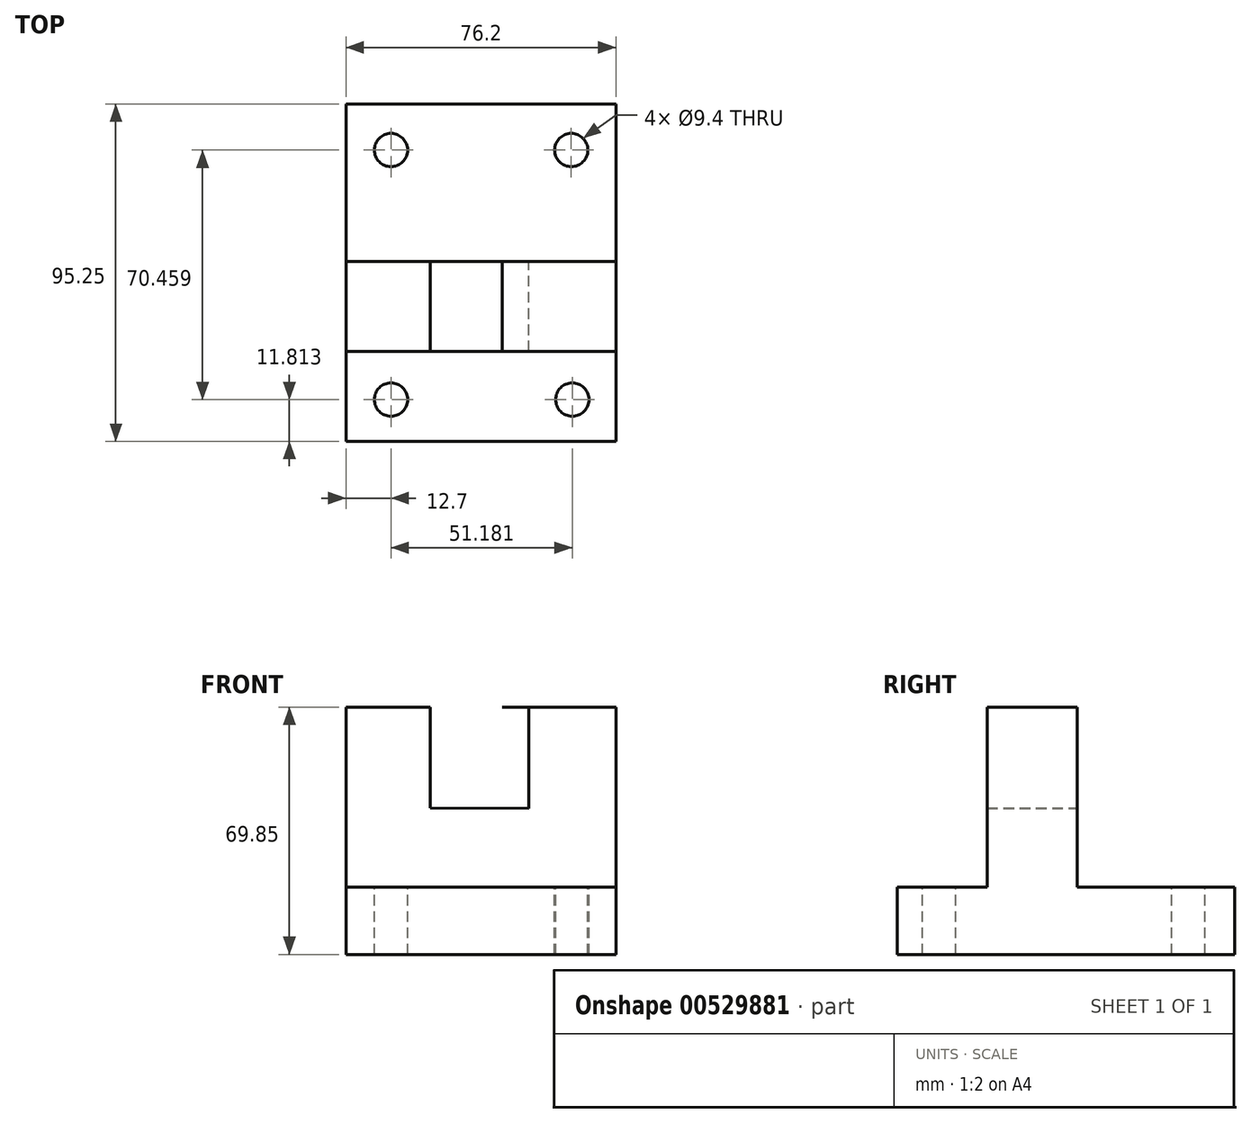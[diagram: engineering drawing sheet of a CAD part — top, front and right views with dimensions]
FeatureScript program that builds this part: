
annotation { "Feature Type Name" : "Feature", "Feature Type Description" : "" }
export const myFeature = defineFeature(function(context is Context, id is Id, definition is map)
    precondition{}
    {
        {
            var Q0;
            Q0=qCreatedBy(makeId("Right.planeOp"),FACE);
            var sketch = newSketch(context, id + "F0", { "sketchPlane" : qUnion([Q0])});
            skPoint(sketch, "E0.start.orphan", {"position": v(-46.47, 48.09) * mm});
            skPoint(sketch, "E1.start.orphan", {"position": v(-22.64, 19.51) * mm});
            skPoint(sketch, "E2.end.orphan", {"position": v(5.9, 19.51) * mm});
            skPoint(sketch, "E3.end.orphan", {"position": v(29.73, 48.09) * mm});
            skLineSegment(sketch, "E4", {"start": v(44.45, -31.82) * mm, "end": v(-50.8, -31.82) * mm});
            skLineSegment(sketch, "E5", {"start": v(-50.8, -31.82) * mm, "end": v(-50.8, -12.77) * mm});
            skLineSegment(sketch, "E6", {"start": v(-50.8, -12.77) * mm, "end": v(-25.4, -12.77) * mm});
            skLineSegment(sketch, "E7", {"start": v(-25.4, -12.77) * mm, "end": v(-25.4, 38.03) * mm});
            skLineSegment(sketch, "E8", {"start": v(-25.4, 38.03) * mm, "end": v(0, 38.03) * mm});
            skLineSegment(sketch, "E9", {"start": v(0, 38.03) * mm, "end": v(0, -12.77) * mm});
            skLineSegment(sketch, "E10", {"start": v(0, -12.77) * mm, "end": v(44.45, -12.77) * mm});
            skLineSegment(sketch, "E11", {"start": v(44.45, -12.77) * mm, "end": v(44.45, -31.82) * mm});
            skSolve(sketch);
        }
        {
            var Q0;
            Q0=makeQuery(id+"F0.imprint","IMPRINT",FACE,{"disambiguationData":[TD([[makeQuery(id+"F0.imprint","IMPRINT",EDGE,{"derivedFrom":sQuery(id+"F0.wireOp",EDGE,"E4")}),-1.0]])]});
            extrude(context, id + "F1", {"entities" : qUnion([Q0]), "depth" : 76.2 * mm, "offsetDistance" : 25.4 * mm});
        }
        {
            var Q0;
            Q0=qCreatedBy(makeId("Front.planeOp"),FACE);
            var sketch = newSketch(context, id + "F2", { "sketchPlane" : qUnion([Q0])});
            skLineSegment(sketch, "E12", {"start": v(51.64, 38.02) * mm, "end": v(51.64, 9.44) * mm});
            skLineSegment(sketch, "E13", {"start": v(0, 38.08) * mm, "end": v(23.83, 38.08) * mm});
            skLineSegment(sketch, "E14", {"start": v(51.64, 38.02) * mm, "end": v(23.83, 38.08) * mm});
            skLineSegment(sketch, "E15", {"start": v(23.83, 38.08) * mm, "end": v(23.83, 9.5) * mm});
            skLineSegment(sketch, "E16", {"start": v(51.64, 9.44) * mm, "end": v(23.83, 9.5) * mm});
            skPoint(sketch, "E17.end.orphan", {"position": v(23.83, 24.1) * mm});
            skLineSegment(sketch, "E18", {"start": v(23.83, 38.08) * mm, "end": v(0, 38.08) * mm});
            skLineSegment(sketch, "E19", {"start": v(75.47, 38.05) * mm, "end": v(51.64, 38.02) * mm});
            skPoint(sketch, "E19.startSnap0", {"position": v(37.73, 38.05) * mm});
            skLineSegment(sketch, "E20", {"start": v(75.8, 43) * mm, "end": v(51.97, 43) * mm});
            skSolve(sketch);
        }
        {
            var Q0;
            Q0=makeQuery(id+"F1.opExtrude","SWEPT_FACE",FACE,{"disambiguationData":[OSD([sQuery(id+"F0.wireOp",EDGE,"E6")])]});
            var sketch = newSketch(context, id + "F3", { "sketchPlane" : qUnion([Q0])});
            skCircle(sketch, "E21", {"center": v(63.88, -38.99) * mm, "radius": 4.7 * mm});
            skCircle(sketch, "E22", {"center": v(12.7, -38.99) * mm, "radius": 4.7 * mm});
            skPoint(sketch, "E23.orphan", {"position": v(0, -38.57) * mm});
            skCircle(sketch, "E24", {"center": v(12.7, 31.47) * mm, "radius": 4.7 * mm});
            skCircle(sketch, "E25", {"center": v(63.57, 31.47) * mm, "radius": 4.7 * mm});
            skPoint(sketch, "E26.end.orphan", {"position": v(63.88, -51.69) * mm});
            skPoint(sketch, "E27.orphan", {"position": v(12.7, -51.69) * mm});
            skPoint(sketch, "E28.end.orphan", {"position": v(0, -38.99) * mm});
            skPoint(sketch, "E29.end.orphan", {"position": v(0, 31.47) * mm});
            skSolve(sketch);
        }
        {
            var Q0;
            Q0=makeQuery(id+"F3.imprint","IMPRINT",FACE,{"disambiguationData":[TD([[makeQuery(id+"F3.imprint","IMPRINT",EDGE,{"derivedFrom":sQuery(id+"F3.wireOp",EDGE,"E25")}),1.0]])]});
            var Q1;
            Q1=makeQuery(id+"F3.imprint","IMPRINT",FACE,{"disambiguationData":[TD([[makeQuery(id+"F3.imprint","IMPRINT",EDGE,{"derivedFrom":sQuery(id+"F3.wireOp",EDGE,"E24")}),1.0]])]});
            var Q2;
            Q2=makeQuery(id+"F3.imprint","IMPRINT",FACE,{"disambiguationData":[TD([[makeQuery(id+"F3.imprint","IMPRINT",EDGE,{"derivedFrom":sQuery(id+"F3.wireOp",EDGE,"E22")}),1.0]])]});
            var Q3;
            Q3=makeQuery(id+"F3.imprint","IMPRINT",FACE,{"disambiguationData":[TD([[makeQuery(id+"F3.imprint","IMPRINT",EDGE,{"derivedFrom":sQuery(id+"F3.wireOp",EDGE,"E21")}),1.0]])]});
            extrude(context, id + "F4", {"entities" : qUnion([Q0, Q1, Q2, Q3]), "operationType" : NewBodyOperationType.REMOVE, "oppositeDirection" : true, "depth" : 19.05 * mm, "offsetDistance" : 25.4 * mm});
        }
        {
            var Q0;
            Q0=makeQuery(id+"F2.imprint","IMPRINT",FACE,{"disambiguationData":[TD([[makeQuery(id+"F2.imprint","IMPRINT",EDGE,{"derivedFrom":sQuery(id+"F2.wireOp",EDGE,"E12")}),-1.0]])]});
            extrude(context, id + "F5", {"entities" : qUnion([Q0]), "operationType" : NewBodyOperationType.REMOVE, "depth" : 26.16 * mm, "offsetDistance" : 25.4 * mm});
        }
    });
